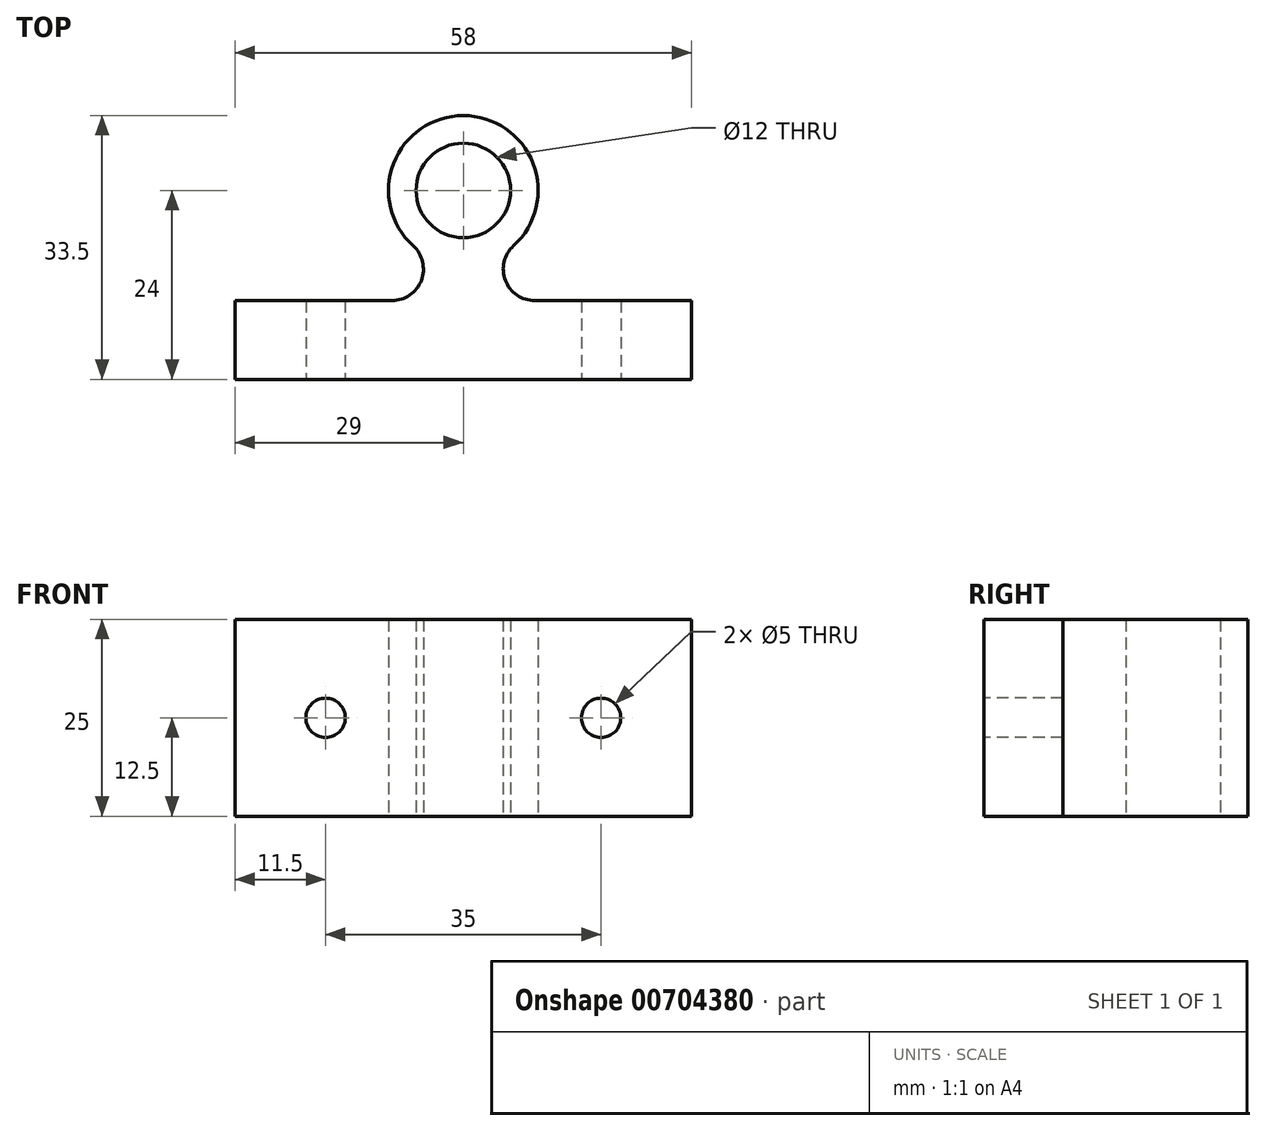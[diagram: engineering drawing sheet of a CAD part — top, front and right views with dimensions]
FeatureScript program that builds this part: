
annotation { "Feature Type Name" : "Feature", "Feature Type Description" : "" }
export const myFeature = defineFeature(function(context is Context, id is Id, definition is map)
    precondition{}
    {
        {
            var Q0;
            Q0=qCreatedBy(makeId("Top.planeOp"),FACE);
            var sketch = newSketch(context, id + "F0", { "sketchPlane" : qUnion([Q0])});
            skLineSegment(sketch, "E0.bottom", {"start": v(-29, 5) * mm, "end": v(-9.07, 5) * mm});
            skLineSegment(sketch, "E0.top", {"start": v(-29, -5) * mm, "end": v(29, -5) * mm});
            skLineSegment(sketch, "E0.left", {"start": v(-29, 5) * mm, "end": v(-29, -5) * mm});
            skLineSegment(sketch, "E0.right", {"start": v(29, 5) * mm, "end": v(29, -5) * mm});
            skCircle(sketch, "E1", {"center": v(0, 19) * mm, "radius": 6 * mm});
            skArc(sketch, "E2", {"start": v(6.38, 11.96) * mm, "mid": v(0, 28.5) * mm, "end": v(-6.38, 11.96) * mm});
            skLineSegment(sketch, "E3.trimOffspring", {"start": v(9.07, 5) * mm, "end": v(29, 5) * mm});
            skArc(sketch, "E4.filletArc", {"start": v(-9.07, 5) * mm, "mid": v(-5.34, 7.56) * mm, "end": v(-6.38, 11.96) * mm});
            skArc(sketch, "E5.MirrorCS", {"start": v(9.07, 5) * mm, "mid": v(5.34, 7.56) * mm, "end": v(6.38, 11.96) * mm});
            skSolve(sketch);
        }
        {
            var Q0;
            Q0=makeQuery(id+"F0.imprint","IMPRINT",FACE,{"disambiguationData":[TD([[makeQuery(id+"F0.imprint","IMPRINT",EDGE,{"derivedFrom":sQuery(id+"F0.wireOp",EDGE,"E0.bottom")}),-1.0]])]});
            extrude(context, id + "F1", {"entities" : qUnion([Q0]), "depth" : 25 * mm, "offsetDistance" : 25 * mm});
        }
        {
            var Q0;
            Q0=makeQuery(id+"F1.opExtrude","SWEPT_FACE",FACE,{"disambiguationData":[OSD([sQuery(id+"F0.wireOp",EDGE,"E0.top")])]});
            var sketch = newSketch(context, id + "F2", { "sketchPlane" : qUnion([Q0])});
            skPoint(sketch, "E6", {"position": v(-17.5, 12.5) * mm});
            skPoint(sketch, "E7", {"position": v(17.5, 12.5) * mm});
            skSolve(sketch);
        }
        {
            var Q0;
            Q0=sQuery(id+"F2.wireOp",VERTEX,"E6");
            var Q1;
            Q1=sQuery(id+"F2.wireOp",VERTEX,"E7");
            var Q2;
            Q2=makeQuery(id+"F1.opExtrude","SWEPT_BODY",BODY,{"disambiguationData":[OSD([sQuery(id+"F0.wireOp",EDGE,"E0.bottom"),sQuery(id+"F0.wireOp",EDGE,"E0.top"),sQuery(id+"F0.wireOp",EDGE,"E0.left"),sQuery(id+"F0.wireOp",EDGE,"E0.right"),sQuery(id+"F0.wireOp",EDGE,"E1"),sQuery(id+"F0.wireOp",EDGE,"E2"),sQuery(id+"F0.wireOp",EDGE,"E3.trimOffspring"),sQuery(id+"F0.wireOp",EDGE,"teZGi27X-nzDp-oRSa-hy7c-2Cnfnbl9mhpk"),sQuery(id+"F0.wireOp",EDGE,"070XQpQS-QudA-2yg8-jCmN-g3vE5bsih7xv"),sQuery(id+"F0.wireOp",EDGE,"f96aeac3-3da2-46b8-9112-7d7eb217ed7d.filletArc"),sQuery(id+"F0.wireOp",EDGE,"b47b4638-460d-4f82-a2fa-4a64d103b366.filletArc"),sQuery(id+"F0.wireOp",EDGE,"612d6255-b389-45d0-b74c-c33b5ef9d83e.filletArc"),sQuery(id+"F0.wireOp",EDGE,"4b7b6995-d7a3-4e43-a67a-86adbe485298.filletArc")])]});
            hole(context, id + "F3", {"style" : HoleStyle.SIMPLE, "endStyle" : HoleEndStyle.THROUGH, "holeDiameter" : 5 * mm, "majorDiameter" : 5 * mm, "tappedDepth" : 12 * mm, "tapClearance" : 3, "locations" : qUnion([Q0, Q1]), "scope" : qUnion([Q2])});
        }
    });
